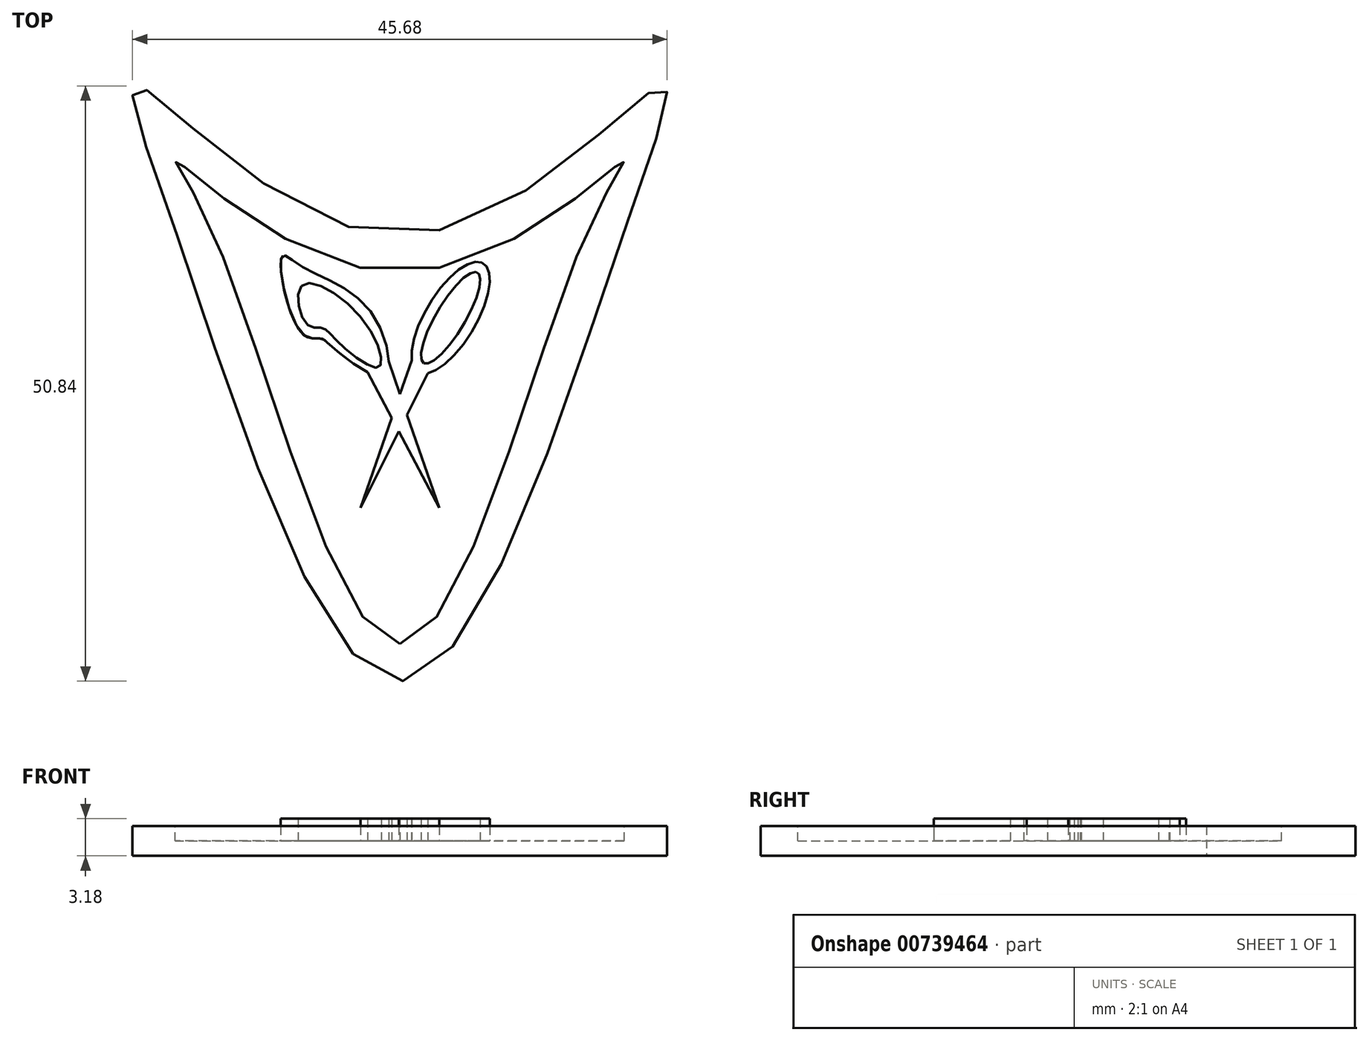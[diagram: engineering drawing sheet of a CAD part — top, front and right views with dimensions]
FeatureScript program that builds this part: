
annotation { "Feature Type Name" : "Feature", "Feature Type Description" : "" }
export const myFeature = defineFeature(function(context is Context, id is Id, definition is map)
    precondition{}
    {
        {
            var Q0;
            Q0=qCreatedBy(makeId("Top.planeOp"),FACE);
            var sketch = newSketch(context, id + "F0", { "sketchPlane" : qUnion([Q0])});
            skFitSpline(sketch, "E0", {"points": [v(-19.05, 0) * mm, v(0, -38.1) * mm, v(19.05, 0) * mm, v(22.23, 12.7) * mm, v(0, 0) * mm, v(-22.23, 12.7) * mm, v(-19.05, 0) * mm]});
            skSolve(sketch);
        }
        {
            var Q0;
            Q0=qSketchRegion(id+"F0",true);
            extrude(context, id + "F1", {"entities" : qUnion([Q0]), "depth" : 2.54 * mm, "offsetDistance" : 25.4 * mm});
        }
        {
            var Q0;
            Q0=makeQuery(id+"F1.opExtrude","CAP_FACE",FACE,{"disambiguationData":[OSD([sQuery(id+"F0.wireOp",EDGE,"E0")])],"isStart":false});
            var sketch = newSketch(context, id + "F2", { "sketchPlane" : qUnion([Q0])});
            skFitSpline(sketch, "E1", {"points": [v(0, -34.93) * mm, v(15.88, 0) * mm, v(19.05, 6.35) * mm, v(0, -3.18) * mm, v(-19.05, 6.35) * mm, v(-15.88, 0) * mm, v(0, -34.93) * mm]});
            skSolve(sketch);
        }
        {
            var Q0;
            Q0=qSketchRegion(id+"F2",true);
            extrude(context, id + "F3", {"entities" : qUnion([Q0]), "operationType" : NewBodyOperationType.REMOVE, "oppositeDirection" : true, "depth" : 1.27 * mm, "offsetDistance" : 25.4 * mm});
        }
        {
            var Q0;
            Q0=makeQuery(id+"F3.boolean.opBoolean","COPY",FACE,{"derivedFrom":makeQuery(id+"F3.opExtrude","CAP_FACE",FACE,{"disambiguationData":[OSD([sQuery(id+"F2.wireOp",EDGE,"E1")])],"isStart":false})});
            var sketch = newSketch(context, id + "F4", { "sketchPlane" : qUnion([Q0])});
            skFitSpline(sketch, "E2", {"points": [v(-8.4, -4.34) * mm, v(-3.27, -7.1) * mm, v(-1.83, -11.3) * mm, v(-5.4, -9) * mm, v(-6.62, -7.93) * mm, v(-7.94, -7.62) * mm, v(-8.4, -4.34) * mm]});
            skFitSpline(sketch, "E3", {"points": [v(-10.08, -1.85) * mm, v(-8.4, -8.35) * mm, v(-6.82, -8.82) * mm, v(-5.97, -9.37) * mm, v(-1.42, -11.96) * mm, v(-2.58, -6.43) * mm, v(-8.4, -2.67) * mm, v(-10.08, -1.85) * mm]});
            skLineSegment(sketch, "E4", {"start": v(-2.76, -11.7) * mm, "end": v(3.37, -23.3) * mm});
            skLineSegment(sketch, "E5", {"start": v(3.37, -23.3) * mm, "end": v(-0.94, -10.8) * mm});
            skEllipse(sketch, "E6", {"center": v(4.35, -7.06) * mm, "majorRadius": 5.42 * mm, "minorRadius": 2.17 * mm, "majorAxis": v(-0.51, -0.86)});
            skEllipse(sketch, "E7", {"center": v(4.35, -7.06) * mm, "majorRadius": 4.5 * mm, "minorRadius": 1.24 * mm, "majorAxis": v(-0.51, -0.86)});
            skLineSegment(sketch, "E8", {"start": v(-3.37, -23.3) * mm, "end": v(2.4, -11.81) * mm});
            skLineSegment(sketch, "E9", {"start": v(-3.37, -23.3) * mm, "end": v(1.02, -10.7) * mm});
            skSolve(sketch);
        }
        {
            var Q0;
            Q0=qSketchRegion(id+"F4",true);
            extrude(context, id + "F5", {"entities" : qUnion([Q0]), "operationType" : NewBodyOperationType.ADD, "depth" : 1.9 * mm, "offsetDistance" : 25.4 * mm});
        }
    });
